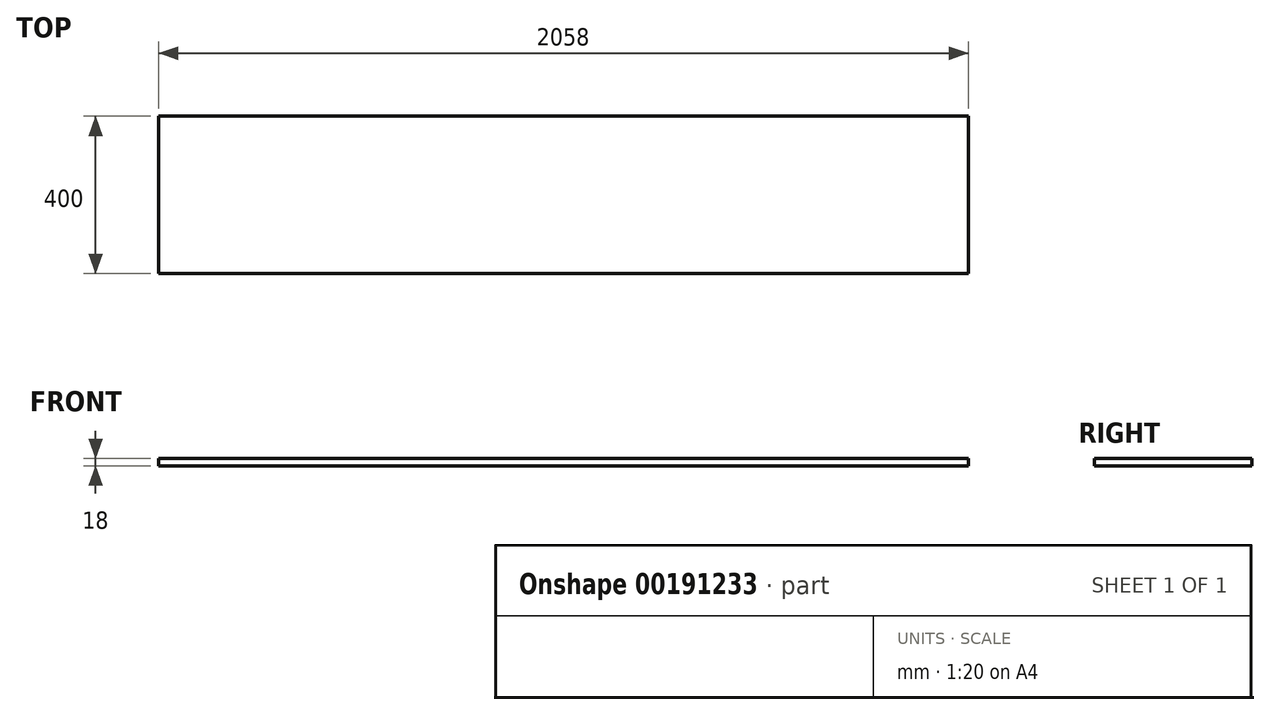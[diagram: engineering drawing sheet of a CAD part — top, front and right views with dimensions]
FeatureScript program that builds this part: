
annotation { "Feature Type Name" : "Feature", "Feature Type Description" : "" }
export const myFeature = defineFeature(function(context is Context, id is Id, definition is map)
    precondition{}
    {
        {
            var Q0;
            Q0=qCreatedBy(makeId("Top.planeOp"),FACE);
            var sketch = newSketch(context, id + "F0", { "sketchPlane" : qUnion([Q0])});
            skLineSegment(sketch, "E0.bottom", {"start": v(0, 0) * mm, "end": v(-2058, 0) * mm});
            skLineSegment(sketch, "E0.top", {"start": v(0, 400) * mm, "end": v(-2058, 400) * mm});
            skLineSegment(sketch, "E0.left", {"start": v(0, 0) * mm, "end": v(0, 400) * mm});
            skLineSegment(sketch, "E0.right", {"start": v(-2058, 0) * mm, "end": v(-2058, 400) * mm});
            skSolve(sketch);
        }
        {
            var Q0;
            Q0 = qSketchRegion(id + "F0", true);
            extrude(context, id + "F1", {"entities" : qUnion([Q0]), "depth" : 18 * mm});
        }
    });
